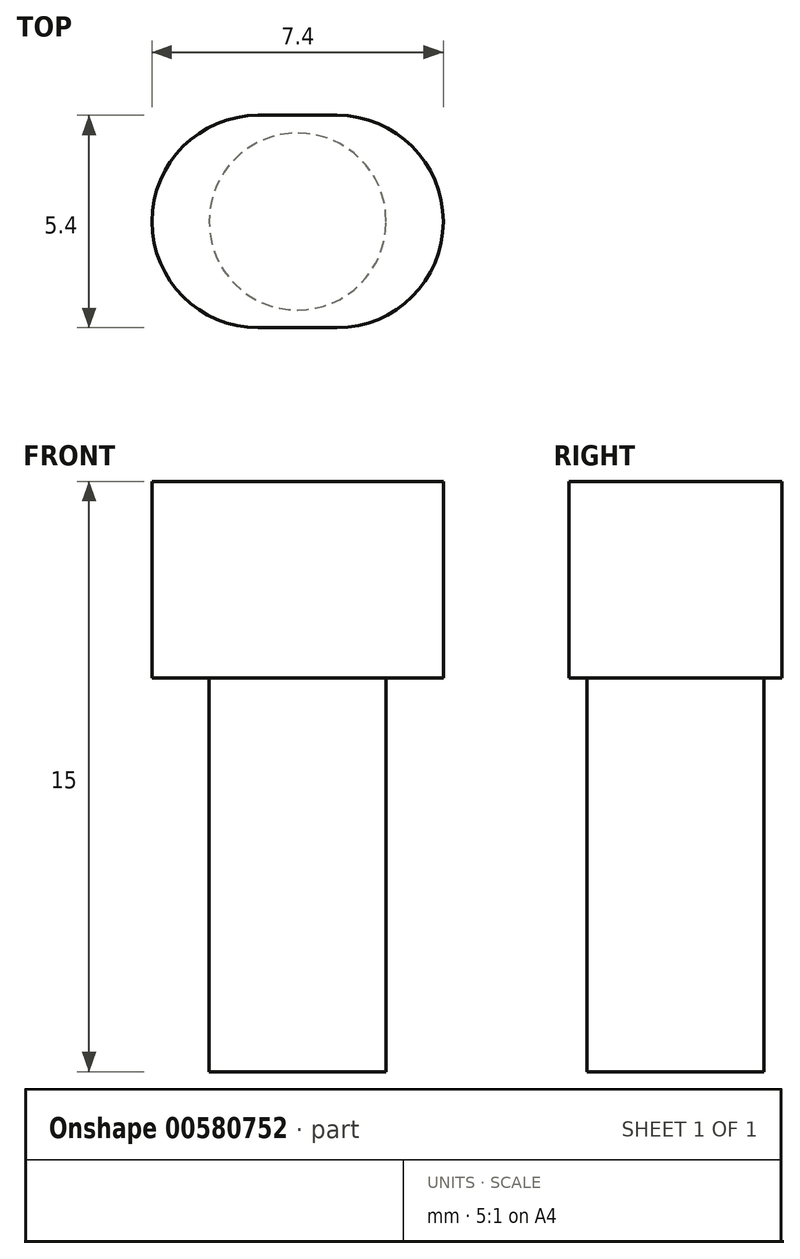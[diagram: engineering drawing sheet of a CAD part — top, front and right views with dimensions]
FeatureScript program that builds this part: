
annotation { "Feature Type Name" : "Feature", "Feature Type Description" : "" }
export const myFeature = defineFeature(function(context is Context, id is Id, definition is map)
    precondition{}
    {
        {
            var Q0;
            Q0=qCreatedBy(makeId("Top.planeOp"),FACE);
            var sketch = newSketch(context, id + "F0", { "sketchPlane" : qUnion([Q0])});
            skLineSegment(sketch, "E0", {"start": v(0, 0) * mm, "end": v(-1, 0) * mm, "construction": true});
            skArc(sketch, "E1", {"start": v(-1, 2.7) * mm, "mid": v(-3.7, 0) * mm, "end": v(-1, -2.7) * mm});
            skLineSegment(sketch, "E2", {"start": v(-1, 2.7) * mm, "end": v(1, 2.7) * mm});
            skLineSegment(sketch, "E3", {"start": v(-1, -2.7) * mm, "end": v(1, -2.7) * mm});
            skArc(sketch, "E4", {"start": v(1, -2.7) * mm, "mid": v(3.7, 0) * mm, "end": v(1, 2.7) * mm});
            skPoint(sketch, "E4.centerSnap0", {"position": v(-0.5, 0) * mm});
            skLineSegment(sketch, "E5", {"start": v(-1, 0) * mm, "end": v(-3.7, 0) * mm, "construction": true});
            skLineSegment(sketch, "E6", {"start": v(0, 0) * mm, "end": v(3.7, 0) * mm, "construction": true});
            skSolve(sketch);
        }
        {
            var Q0;
            Q0=qSketchRegion(id+"F0",true);
            extrude(context, id + "F1", {"entities" : qUnion([Q0]), "depth" : 5 * mm, "offsetDistance" : 25 * mm});
        }
        {
            var Q0;
            Q0=makeQuery(id+"F1.opExtrude","CAP_FACE",FACE,{"disambiguationData":[OSD([sQuery(id+"F0.wireOp",EDGE,"E1"),sQuery(id+"F0.wireOp",EDGE,"E2"),sQuery(id+"F0.wireOp",EDGE,"E3"),sQuery(id+"F0.wireOp",EDGE,"E4")])],"isStart":true});
            var sketch = newSketch(context, id + "F2", { "sketchPlane" : qUnion([Q0])});
            skCircle(sketch, "E7", {"center": v(0, 0) * mm, "radius": 2.25 * mm});
            skSolve(sketch);
        }
        {
            var Q0;
            Q0=qSketchRegion(id+"F2",true);
            extrude(context, id + "F3", {"entities" : qUnion([Q0]), "operationType" : NewBodyOperationType.ADD, "depth" : 10 * mm, "offsetDistance" : 25 * mm});
        }
    });
